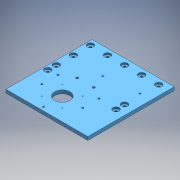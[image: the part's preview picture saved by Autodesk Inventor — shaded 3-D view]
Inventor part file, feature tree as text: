
AUTODESK INVENTOR PART (.ipt)
format: ipt  version: 2016 (Build 200138000, 138)  size: 201,216 bytes
history: native  units: mm
features: sketch x7, hole x5, extrude x2
ambient origin geometry x8: Origin, YZ Plane, XZ Plane, XY Plane, X Axis, Y Axis, Z Axis, Center Point
bodies: Solid1 (feature_tree)
feature tree (14):
  extrude  "baseExtrusion"  Depth=240.0mm
  extrude  "objectiveExtrusion"  Depth=252.5mm
  hole  "60mmCageRodThread"  [1 undecoded]
  hole  "m6BreadoardMountingHoles"  [1 undecoded]
  hole  "m4MirrorTLMountingHoles"  [1 undecoded]
  hole  "m6objectiveHolderMountingHoles"  [1 undecoded]
  hole  "filterwheelMountingHoles"  [1 undecoded]
  sketch  "Sketch1"  dims[d0=240.0mm d1=140.0mm]
  sketch  "Sketch2"  dims[d2=252.5mm d3=135.0mm]
  sketch  "Sketch3"  dims[d4=10.2mm d5=0.0mm d6=45.0mm]
  sketch  "Sketch4"  dims[d7=65.0mm d8=9.2mm d9=0.0mm]
  sketch  "Sketch5"  dims[d10=60.0mm d11=60.0mm]
  sketch  "Sketch6"  dims[d12=30.0mm]
  sketch  "Sketch7"  dims[d13=2.156mm d14=5.69mm d15=4.0mm d16=2.0mm d17=90.0deg d18=8.865mm d19=20.594885mm d20=200.0mm d21=100.0mm d23=70.0mm d24=6.6mm d25=5.69mm d26=18.0mm d27=4.8mm d28=90.0deg d29=8.865mm d30=20.594885mm d31=110.0mm d33=4.5mm d34=5.69mm d35=13.0mm d36=3.4mm d37=90.0deg d38=8.865mm d39=20.594885mm d40=8.4mm d41=30.0mm d42=120.0mm d43=60.0mm d44=47.5mm d45=55.0mm d46=30.0mm d47=4.917mm d48=12.0mm d49=4.0mm d50=2.0mm d51=90.0deg d52=17.1mm d53=20.594885mm d54=48.5mm d55=24.25mm d56=68.0mm d57=6.6mm d58=12.0mm d59=10.0mm d60=4.8mm d61=90.0deg d62=17.1mm d63=20.594885mm d72=98.9mm d73=10.2mm d74=100.0mm d75=25.0mm d76=50.0mm d77=50.0mm d78=12.5mm d79=50.0mm]
note: 5 required parameter values undecoded (feature->parameter linkage not recoverable at this tier; creation-order binding heuristic only, values carry confidence <= 0.55)
